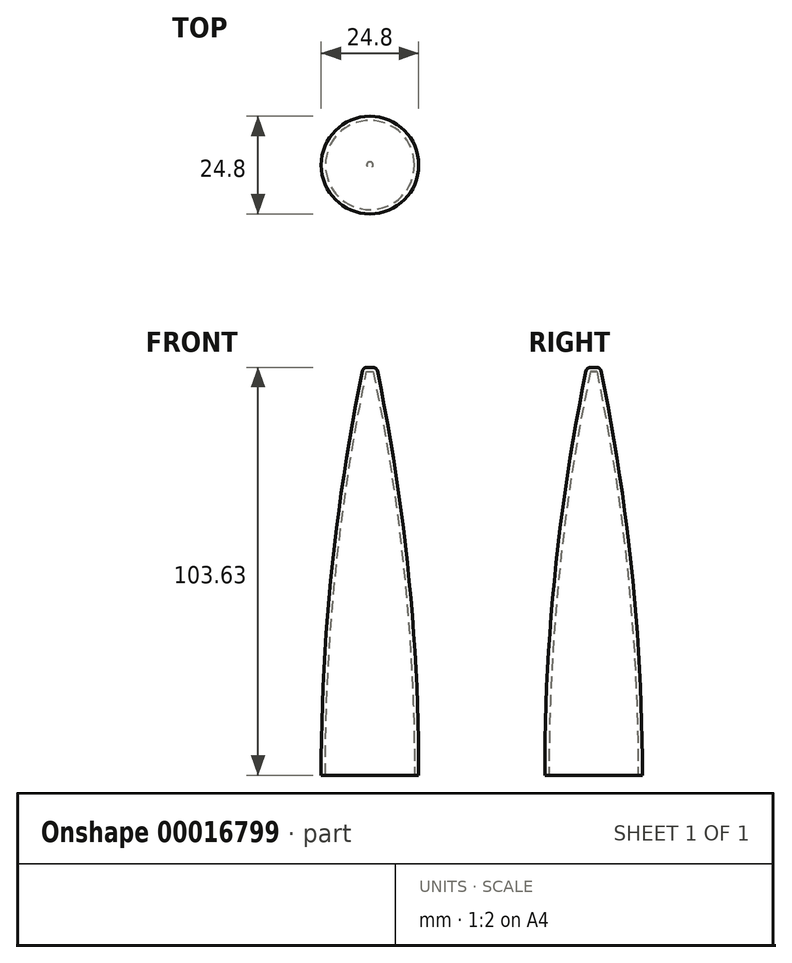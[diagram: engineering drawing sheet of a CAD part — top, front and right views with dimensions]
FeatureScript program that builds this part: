
annotation { "Feature Type Name" : "Feature", "Feature Type Description" : "" }
export const myFeature = defineFeature(function(context is Context, id is Id, definition is map)
    precondition{}
    {
        {
            var Q0;
            Q0=qCreatedBy(makeId("Front.planeOp"),FACE);
            var sketch = newSketch(context, id + "F0", { "sketchPlane" : qUnion([Q0])});
            skLineSegment(sketch, "E0", {"start": v(0, 0) * mm, "end": v(0, 103.63) * mm});
            skLineSegment(sketch, "E1", {"start": v(0, 103.63) * mm, "end": v(0.83, 103.63) * mm});
            skLineSegment(sketch, "E2", {"start": v(0, 0) * mm, "end": v(12.4, 0) * mm});
            skArc(sketch, "E3", {"start": v(12.4, 0) * mm, "mid": v(9.76, 51.66) * mm, "end": v(1.87, 102.78) * mm});
            skLineSegment(sketch, "E4", {"start": v(1.87, 102.78) * mm, "end": v(0, 102.78) * mm, "construction": true});
            skArc(sketch, "E5", {"start": v(1.87, 102.78) * mm, "mid": v(1.5, 103.4) * mm, "end": v(0.83, 103.63) * mm});
            skArc(sketch, "E6", {"start": v(11.32, 0) * mm, "mid": v(8.68, 51.54) * mm, "end": v(0.81, 102.55) * mm});
            skLineSegment(sketch, "E7", {"start": v(0, 102.55) * mm, "end": v(0.81, 102.55) * mm});
            skSolve(sketch);
        }
        {
            var Q0;
            {var subQ4=sQuery(id+"F0.wireOp",EDGE,"E1");Q0=makeQuery(id+"F0.imprint","IMPRINT",FACE,{"disambiguationData":[TD([[makeQuery(id+"F0.imprint","IMPRINT",EDGE,{"derivedFrom":subQ4}),-1.0]])]});}
            var Q1;
            Q1=sQuery(id+"F0.wireOp",EDGE,"E0");
            revolve(context, id + "F1", {"entities" : qUnion([Q0]), "axis" : qUnion([Q1]), "revolveType" : RevolveType.FULL});
        }
    });
